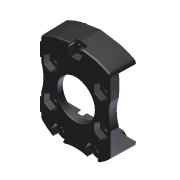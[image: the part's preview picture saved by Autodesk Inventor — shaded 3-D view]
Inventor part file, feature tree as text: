
AUTODESK INVENTOR PART (.ipt)
format: ipt  version: 2015 (Build 190159000, 159)  size: 3,599,872 bytes
history: native  units: in
note: dims shown in document units (in); Inventor stores cm internally (conversion verified against a paired STEP export)
features: chamfer x1, other x1, imported_body x1
ambient origin geometry x8: Origin, YZ Plane, XZ Plane, XY Plane, X Axis, Y Axis, Z Axis, Center Point
bodies: Body1 (feature_tree)
feature tree (3):
  chamfer  "Chamfer2"  [1 undecoded]
  other  "217-4155-001 Rev6.ipt1"
  imported_body  "Base1"
note: 1 required parameter value undecoded (feature->parameter linkage not recoverable at this tier; creation-order binding heuristic only, values carry confidence <= 0.55)
